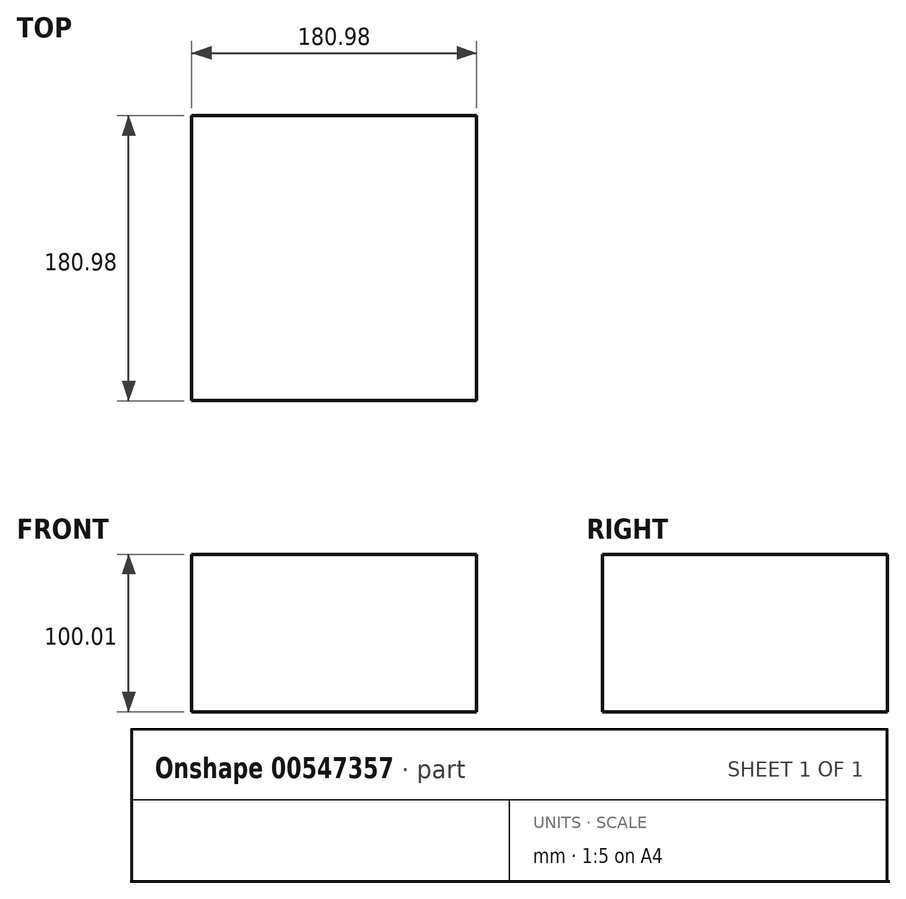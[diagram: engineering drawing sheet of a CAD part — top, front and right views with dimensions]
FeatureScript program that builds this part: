
annotation { "Feature Type Name" : "Feature", "Feature Type Description" : "" }
export const myFeature = defineFeature(function(context is Context, id is Id, definition is map)
    precondition{}
    {
        {
            var Q0;
            Q0=qCreatedBy(makeId("Top.planeOp"),FACE);
            var sketch = newSketch(context, id + "F0", { "sketchPlane" : qUnion([Q0])});
            skLineSegment(sketch, "E0.bottom", {"start": v(90.49, 90.49) * mm, "end": v(-90.49, 90.49) * mm});
            skLineSegment(sketch, "E0.top", {"start": v(90.49, -90.49) * mm, "end": v(-90.49, -90.49) * mm});
            skLineSegment(sketch, "E0.left", {"start": v(90.49, 90.49) * mm, "end": v(90.49, -90.49) * mm});
            skLineSegment(sketch, "E0.right", {"start": v(-90.49, 90.49) * mm, "end": v(-90.49, -90.49) * mm});
            skPoint(sketch, "E0.middle", {"position": v(0, 0) * mm});
            skSolve(sketch);
        }
        {
            var Q0;
            Q0=makeQuery(id+"F0.imprint","IMPRINT",FACE,{"disambiguationData":[TD([[makeQuery(id+"F0.imprint","IMPRINT",EDGE,{"derivedFrom":sQuery(id+"F0.wireOp",EDGE,"E0.bottom")}),1.0]])]});
            extrude(context, id + "F1", {"entities" : qUnion([Q0]), "depth" : 100.01 * mm, "offsetDistance" : 25.4 * mm});
        }
    });
